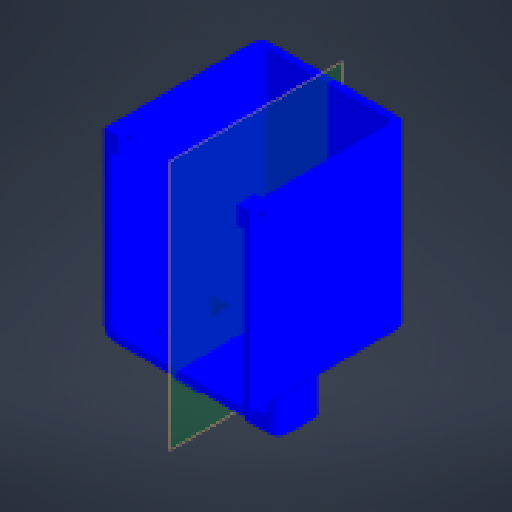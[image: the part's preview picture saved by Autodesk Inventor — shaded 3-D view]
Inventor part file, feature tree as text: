
AUTODESK INVENTOR PART (.ipt)
format: ipt  version: 2024 (Build 280153000, 153)  size: 294,912 bytes
history: native  units: mm
features: other x13, extrude x9, sketch x9, reference x6, fillet x3, mirror x1, projected_geometry x1
ambient origin geometry x8: Origin, YZ Plane, XZ Plane, XY Plane, X Axis, Y Axis, Z Axis, Center Point
bodies: Body1 (feature_tree)
feature tree (42):
  other  "Твердое тело1"
  extrude  "Выдавливание1"  Depth=4.0mm
  extrude  "Выдавливание2"  Depth=15.0mm
  fillet  "Сопряжение1"  Radius=20.0mm
  extrude  "Выдавливание3"  Depth=20.0mm
  extrude  "Выдавливание4"  Depth=4.0mm TaperAngle=0.0deg
  extrude  "Выдавливание5"  Depth=3.0mm
  extrude  "Выдавливание6"  Depth=3.0mm
  extrude  "Выдавливание7"  Depth=17.0mm TaperAngle=0.0deg
  extrude  "Выдавливание8"  Depth=4.0mm
  other  "РабПлоскость1"
  mirror  "Зеркальное отражение1"
  fillet  "Сопряжение3"  Radius=3.0mm
  fillet  "Сопряжение4"  [1 undecoded]
  extrude  "Выдавливание9"  Depth=65.0mm
  sketch  "Эскиз1"
  sketch  "Эскиз2"
  sketch  "Эскиз3"
  sketch  "Эскиз4"
  reference  "Ссылка1"
  reference  "Ссылка2"
  sketch  "Эскиз5"
  sketch  "Эскиз6"
  projected_geometry  "Спроецированная петля3"
  sketch  "Эскиз7"
  sketch  "Эскиз8"
  sketch  "Эскиз9"
  reference  "Ссылка3"
  reference  "Ссылка4"
  reference  "Ссылка5"
  reference  "Ссылка6"
  parser-record x2  (decoder bookkeeping rows leaked as tree rows — omitted from the tree; the rows remain in map.json)
  other  "main_assembly.iam"
  other  "back_box_asembly:1"
  other  "back_box:1"
  other  "tail_box_asembly.iam"
  other  "bts_asembly:1"
  other  "DIN 934 - заменено на DIN EN 24032/28673/28674 M3:3"
  other  "DIN 934 - заменено на DIN EN 24032/28673/28674 M3:1"
  other  "DIN 934 - заменено на DIN EN 24032/28673/28674 M3:2"
  other  "DIN 934 - заменено на DIN EN 24032/28673/28674 M3:4"
note: 1 required parameter value undecoded (feature->parameter linkage not recoverable at this tier; creation-order binding heuristic only, values carry confidence <= 0.55)
note: 2 file-system paths scrubbed to <path> (originals preserved in map.json)
